annotation { "Feature Type Name" : "Feature", "Feature Type Description" : "" }
export const myFeature = defineFeature(function(context is Context, id is Id, definition is map)
    precondition{}
    {
        {
            var Q0;
            Q0=qCreatedBy(makeId("Top.planeOp"),FACE);
            var sketch = newSketch(context, id + "F0", { "sketchPlane" : qUnion([Q0])});
            skLineSegment(sketch, "E0.bottom", {"start": v(-202.47, -68.03) * mm, "end": v(265.53, -68.03) * mm});
            skLineSegment(sketch, "E0.top", {"start": v(-202.47, 94.32) * mm, "end": v(265.53, 94.32) * mm});
            skLineSegment(sketch, "E0.left", {"start": v(-202.47, -68.03) * mm, "end": v(-202.47, 94.32) * mm});
            skLineSegment(sketch, "E0.right", {"start": v(265.53, -68.03) * mm, "end": v(265.53, 94.32) * mm});
            skSolve(sketch);
        }
        {
            var Q0;
            Q0=qSketchRegion(id+"F0",true);
            extrude(context, id + "F1", {"entities" : qUnion([Q0]), "depth" : 9.65 * mm});
        }
        {
            var Q0;
            Q0=makeQuery(id+"F1.opExtrude","CAP_FACE",FACE,{"disambiguationData":[OSD([sQuery(id+"F0.wireOp",EDGE,"E0.bottom"),sQuery(id+"F0.wireOp",EDGE,"E0.top"),sQuery(id+"F0.wireOp",EDGE,"E0.left"),sQuery(id+"F0.wireOp",EDGE,"E0.right")])],"isStart":false});
            cPlane(context, id + "F2", {"entities" : qUnion([Q0]), "cplaneType" : CPlaneType.OFFSET, "offset" : 12.7 * mm, "width" : 152.4 * mm, "height" : 152.4 * mm});
        }
        {
            var Q0;
            Q0=qCreatedBy(id+"F2.planeOp",FACE);
            var sketch = newSketch(context, id + "F3", { "sketchPlane" : qUnion([Q0])});
            skLineSegment(sketch, "E1.bottom", {"start": v(-42.18, 47.21) * mm, "end": v(-23.05, 47.21) * mm});
            skLineSegment(sketch, "E1.top", {"start": v(-42.18, -43.63) * mm, "end": v(-23.05, -43.63) * mm});
            skLineSegment(sketch, "E1.left", {"start": v(-42.18, 47.21) * mm, "end": v(-42.18, -43.63) * mm});
            skLineSegment(sketch, "E1.right", {"start": v(-23.05, 47.21) * mm, "end": v(-23.05, -43.63) * mm});
            skLineSegment(sketch, "E2.bottom", {"start": v(0.45, 47.21) * mm, "end": v(116.8, 47.21) * mm});
            skLineSegment(sketch, "E2.top", {"start": v(0.45, -43.63) * mm, "end": v(116.8, -43.63) * mm});
            skLineSegment(sketch, "E2.left", {"start": v(0.45, 47.21) * mm, "end": v(0.45, -43.63) * mm});
            skLineSegment(sketch, "E2.right", {"start": v(116.8, 47.21) * mm, "end": v(116.8, -43.63) * mm});
            skLineSegment(sketch, "E3.bottom", {"start": v(-151.75, -3.79) * mm, "end": v(-59.7, -3.79) * mm});
            skLineSegment(sketch, "E3.top", {"start": v(-151.75, -43.63) * mm, "end": v(-59.7, -43.63) * mm});
            skLineSegment(sketch, "E3.left", {"start": v(-151.75, -3.79) * mm, "end": v(-151.75, -43.63) * mm});
            skLineSegment(sketch, "E3.right", {"start": v(-59.7, -3.79) * mm, "end": v(-59.7, -43.63) * mm});
            skLineSegment(sketch, "E4.bottom", {"start": v(-151.75, 47.21) * mm, "end": v(-59.7, 47.21) * mm});
            skLineSegment(sketch, "E4.top", {"start": v(-151.75, 9.76) * mm, "end": v(-59.7, 9.76) * mm});
            skLineSegment(sketch, "E4.left", {"start": v(-151.75, 47.21) * mm, "end": v(-151.75, 9.76) * mm});
            skLineSegment(sketch, "E4.right", {"start": v(-59.7, 47.21) * mm, "end": v(-59.7, 9.76) * mm});
            skLineSegment(sketch, "E5.bottom", {"start": v(144.29, 46.82) * mm, "end": v(185.33, 46.82) * mm});
            skLineSegment(sketch, "E5.top", {"start": v(144.29, -43.63) * mm, "end": v(185.33, -43.63) * mm});
            skLineSegment(sketch, "E5.left", {"start": v(144.29, 46.82) * mm, "end": v(144.29, -43.63) * mm});
            skLineSegment(sketch, "E5.right", {"start": v(185.33, 46.82) * mm, "end": v(185.33, -43.63) * mm});
            skText(sketch, "E6", { "text": "Microprocessor", "fontName": "OpenSans-Bold.ttf"});
            skText(sketch, "E7", { "text": "Laser Driver", "fontName": "OpenSans-Bold.ttf"});
            skText(sketch, "E8", { "text": "Detector \nReadout", "fontName": "OpenSans-Bold.ttf"});
            skText(sketch, "E9", { "text": "Laser Array", "fontName": "OpenSans-Bold.ttf"});
            skText(sketch, "E10", { "text": "Detector Matrix", "fontName": "OpenSans-Bold.ttf"});
            skLineSegment(sketch, "E11.bottom", {"start": v(-202.55, 64.45) * mm, "end": v(-189.27, 64.45) * mm});
            skLineSegment(sketch, "E11.top", {"start": v(-202.55, 28.92) * mm, "end": v(-189.27, 28.92) * mm});
            skLineSegment(sketch, "E11.left", {"start": v(-202.55, 64.45) * mm, "end": v(-202.55, 28.92) * mm});
            skLineSegment(sketch, "E11.right", {"start": v(-189.27, 64.45) * mm, "end": v(-189.27, 28.92) * mm});
            const initialGuessF3  = {"E6": [-0.15175, 0.02577, 1, 0, 0.00854], "E7": [-0.14372, -0.02662, 1, 0, 0.00854], "E8": [0.16063, -0.0254, 0, 1, 0.00854], "E9": [-0.02817, -0.03238, 0, 1, 0.00854], "E10": [0.01132, -0.00132, 1, 0, 0.00854]};
            skSetInitialGuess(sketch, initialGuessF3);
            skSolve(sketch);
        }
        {
            var Q0;
            Q0 = qSketchRegion(id + "F3", true);
            extrude(context, id + "F4", {"entities" : qUnion([Q0]), "depth" : 7.11 * mm, "hasSecondDirection" : true, "secondDirectionOppositeDirection" : true, "secondDirectionDepth" : 8.9 * mm});
        }
    });